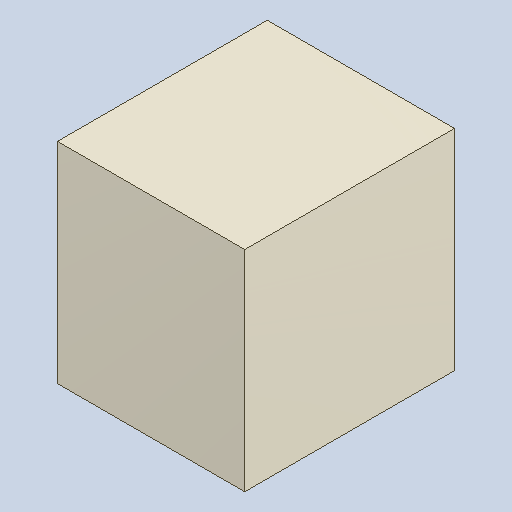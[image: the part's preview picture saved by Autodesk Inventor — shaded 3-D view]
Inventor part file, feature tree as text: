
AUTODESK INVENTOR PART (.ipt)
format: ipt  version: 2023.4 (Build 274418000, 418)  size: 82,944 bytes
history: native  units: mm
features: extrude x1
ambient origin geometry x8: Origin, YZ Plane, XZ Plane, XY Plane, X Axis, Y Axis, Z Axis, Center Point
bodies: Solid1 (feature_tree)
feature tree (1):
  extrude  "Extruded_5"  [1 undecoded]
note: 1 required parameter value undecoded (feature->parameter linkage not recoverable at this tier; creation-order binding heuristic only, values carry confidence <= 0.55)
